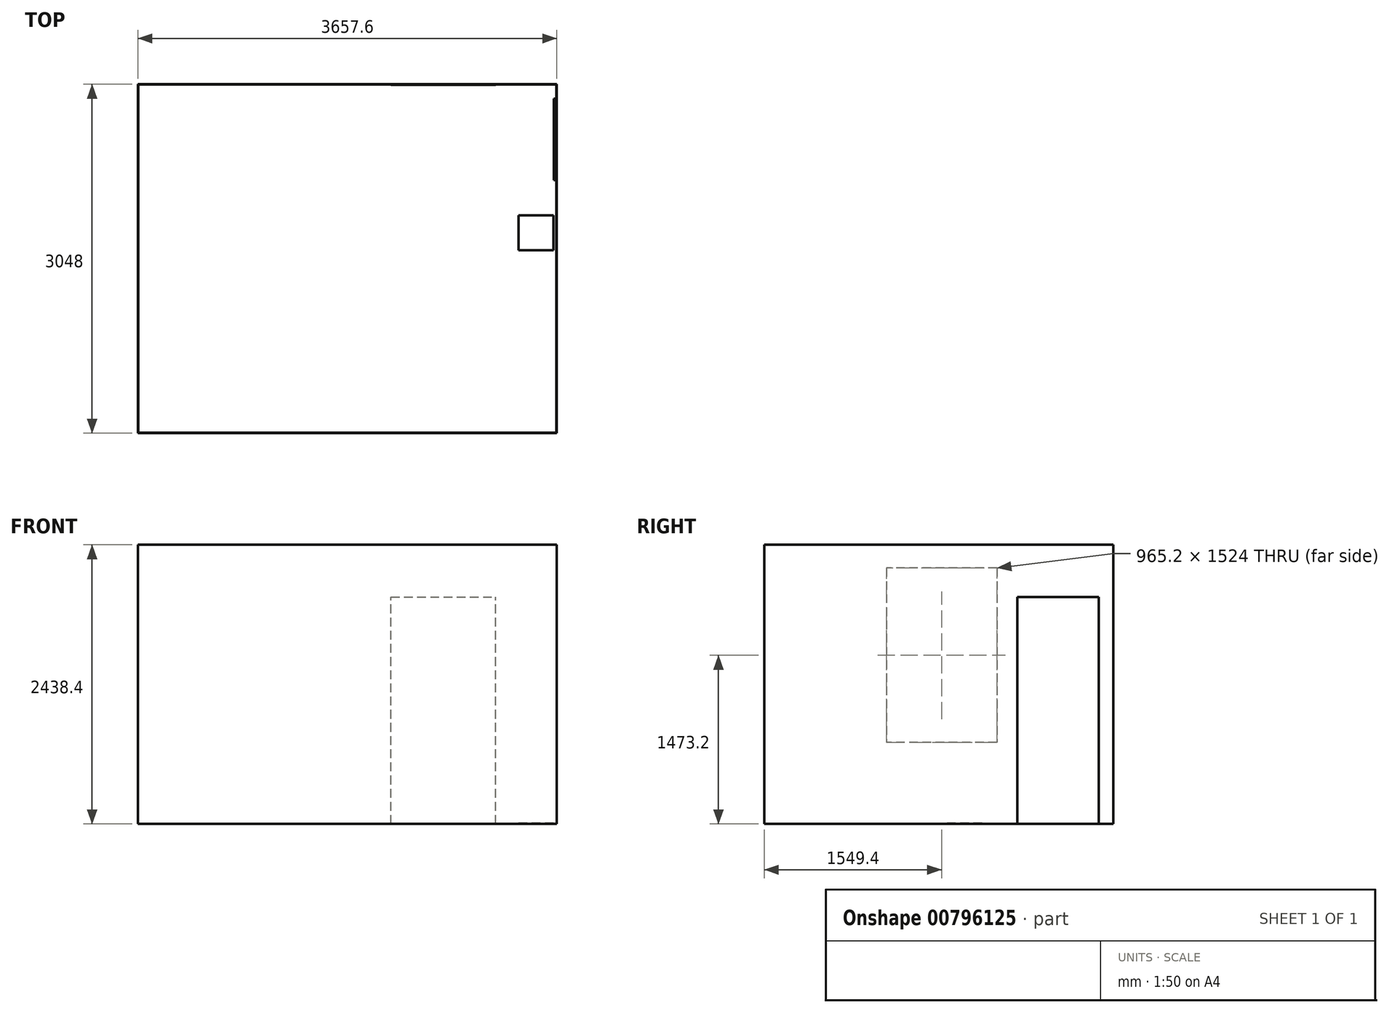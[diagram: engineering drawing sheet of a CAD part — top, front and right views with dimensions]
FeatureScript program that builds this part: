
annotation { "Feature Type Name" : "Feature", "Feature Type Description" : "" }
export const myFeature = defineFeature(function(context is Context, id is Id, definition is map)
    precondition{}
    {
        {
            var Q0;
            Q0=qCreatedBy(makeId("Top.planeOp"),FACE);
            var sketch = newSketch(context, id + "F0", { "sketchPlane" : qUnion([Q0])});
            skLineSegment(sketch, "E0.bottom", {"start": v(0, 0) * mm, "end": v(3657.6, 0) * mm});
            skLineSegment(sketch, "E0.top", {"start": v(0, 3048) * mm, "end": v(3657.6, 3048) * mm});
            skLineSegment(sketch, "E0.left", {"start": v(0, 0) * mm, "end": v(0, 3048) * mm});
            skLineSegment(sketch, "E0.right", {"start": v(3657.6, 0) * mm, "end": v(3657.6, 3048) * mm});
            skSolve(sketch);
        }
        {
            var Q0;
            Q0 = qSketchRegion(id + "F0", true);
            extrude(context, id + "F1", {"entities" : qUnion([Q0]), "depth" : 2438.4 * mm, "offsetDistance" : 25.4 * mm});
        }
        {
            var Q0;
            Q0=makeQuery(id+"F1.opExtrude","CAP_FACE",FACE,{"disambiguationData":[OSD([sQuery(id+"F0.wireOp",EDGE,"E0.bottom"),sQuery(id+"F0.wireOp",EDGE,"E0.top"),sQuery(id+"F0.wireOp",EDGE,"E0.left"),sQuery(id+"F0.wireOp",EDGE,"E0.right")])],"isStart":false});
            shell(context, id + "F2", {"entities" : qUnion([Q0]), "thickness" : 2.54 * mm});
        }
        {
            var Q0;
            Q0=makeQuery(id+"F1.opExtrude","SWEPT_FACE",FACE,{"disambiguationData":[OSD([sQuery(id+"F0.wireOp",EDGE,"E0.right")])]});
            var sketch = newSketch(context, id + "F3", { "sketchPlane" : qUnion([Q0])});
            skLineSegment(sketch, "E1.bottom", {"start": v(2921, 0) * mm, "end": v(2209.8, 0) * mm});
            skLineSegment(sketch, "E1.top", {"start": v(2921, 1981.2) * mm, "end": v(2209.8, 1981.2) * mm});
            skLineSegment(sketch, "E1.left", {"start": v(2921, 0) * mm, "end": v(2921, 1981.2) * mm});
            skLineSegment(sketch, "E1.right", {"start": v(2209.8, 0) * mm, "end": v(2209.8, 1981.2) * mm});
            skSolve(sketch);
        }
        {
            var Q0;
            Q0 = qSketchRegion(id + "F3", true);
            extrude(context, id + "F4", {"entities" : qUnion([Q0]), "operationType" : NewBodyOperationType.REMOVE, "oppositeDirection" : true, "depth" : 25.4 * mm, "offsetDistance" : 25.4 * mm});
        }
        {
            var Q0;
            Q0=makeQuery(id+"F1.opExtrude","SWEPT_FACE",FACE,{"disambiguationData":[OSD([sQuery(id+"F0.wireOp",EDGE,"E0.left")])]});
            var sketch = newSketch(context, id + "F5", { "sketchPlane" : qUnion([Q0])});
            skLineSegment(sketch, "E2.bottom", {"start": v(-2032, 2235.2) * mm, "end": v(-1066.8, 2235.2) * mm});
            skLineSegment(sketch, "E2.top", {"start": v(-2032, 711.2) * mm, "end": v(-1066.8, 711.2) * mm});
            skLineSegment(sketch, "E2.left", {"start": v(-2032, 2235.2) * mm, "end": v(-2032, 711.2) * mm});
            skLineSegment(sketch, "E2.right", {"start": v(-1066.8, 2235.2) * mm, "end": v(-1066.8, 711.2) * mm});
            skSolve(sketch);
        }
        {
            var Q0;
            Q0 = qSketchRegion(id + "F5", true);
            extrude(context, id + "F6", {"entities" : qUnion([Q0]), "operationType" : NewBodyOperationType.REMOVE, "oppositeDirection" : true, "depth" : 25.4 * mm, "offsetDistance" : 25.4 * mm});
        }
        {
            var Q0;
            Q0=makeQuery(id+"F2.opShell","OFFSET_FACE",FACE,{"disambiguationData":[OSD([sQuery(id+"F0.wireOp",EDGE,"E0.bottom"),sQuery(id+"F0.wireOp",EDGE,"E0.top"),sQuery(id+"F0.wireOp",EDGE,"E0.left"),sQuery(id+"F0.wireOp",EDGE,"E0.right")])]});
            var sketch = newSketch(context, id + "F7", { "sketchPlane" : qUnion([Q0])});
            skLineSegment(sketch, "E3.bottom", {"start": v(3629.66, 1902.46) * mm, "end": v(3324.86, 1902.46) * mm});
            skLineSegment(sketch, "E3.top", {"start": v(3629.66, 1597.66) * mm, "end": v(3324.86, 1597.66) * mm});
            skLineSegment(sketch, "E3.left", {"start": v(3629.66, 1902.46) * mm, "end": v(3629.66, 1597.66) * mm});
            skLineSegment(sketch, "E3.right", {"start": v(3324.86, 1902.46) * mm, "end": v(3324.86, 1597.66) * mm});
            skSolve(sketch);
        }
        {
            var Q0;
            Q0=makeQuery(id+"F7.imprint","IMPRINT",FACE,{"disambiguationData":[TD([[makeQuery(id+"F7.imprint","IMPRINT",EDGE,{"derivedFrom":sQuery(id+"F7.wireOp",EDGE,"E3.bottom")}),1.0]])]});
            extrude(context, id + "F8", {"entities" : qUnion([Q0]), "operationType" : NewBodyOperationType.ADD, "depth" : 6.35 * mm, "offsetDistance" : 25.4 * mm});
        }
        {
            var Q0;
            Q0=makeQuery(id+"F1.opExtrude","SWEPT_FACE",FACE,{"disambiguationData":[OSD([sQuery(id+"F0.wireOp",EDGE,"E0.top")])]});
            var sketch = newSketch(context, id + "F9", { "sketchPlane" : qUnion([Q0])});
            skLineSegment(sketch, "E4.bottom", {"start": v(-2209.8, 0) * mm, "end": v(-3124.2, 0) * mm});
            skLineSegment(sketch, "E4.top", {"start": v(-2209.8, 1981.2) * mm, "end": v(-3124.2, 1981.2) * mm});
            skLineSegment(sketch, "E4.left", {"start": v(-2209.8, 0) * mm, "end": v(-2209.8, 1981.2) * mm});
            skLineSegment(sketch, "E4.right", {"start": v(-3124.2, 0) * mm, "end": v(-3124.2, 1981.2) * mm});
            skSolve(sketch);
        }
        {
            var Q0;
            Q0 = qSketchRegion(id + "F9", true);
            extrude(context, id + "F10", {"entities" : qUnion([Q0]), "operationType" : NewBodyOperationType.REMOVE, "oppositeDirection" : true, "depth" : 6.35 * mm, "offsetDistance" : 25.4 * mm});
        }
    });
